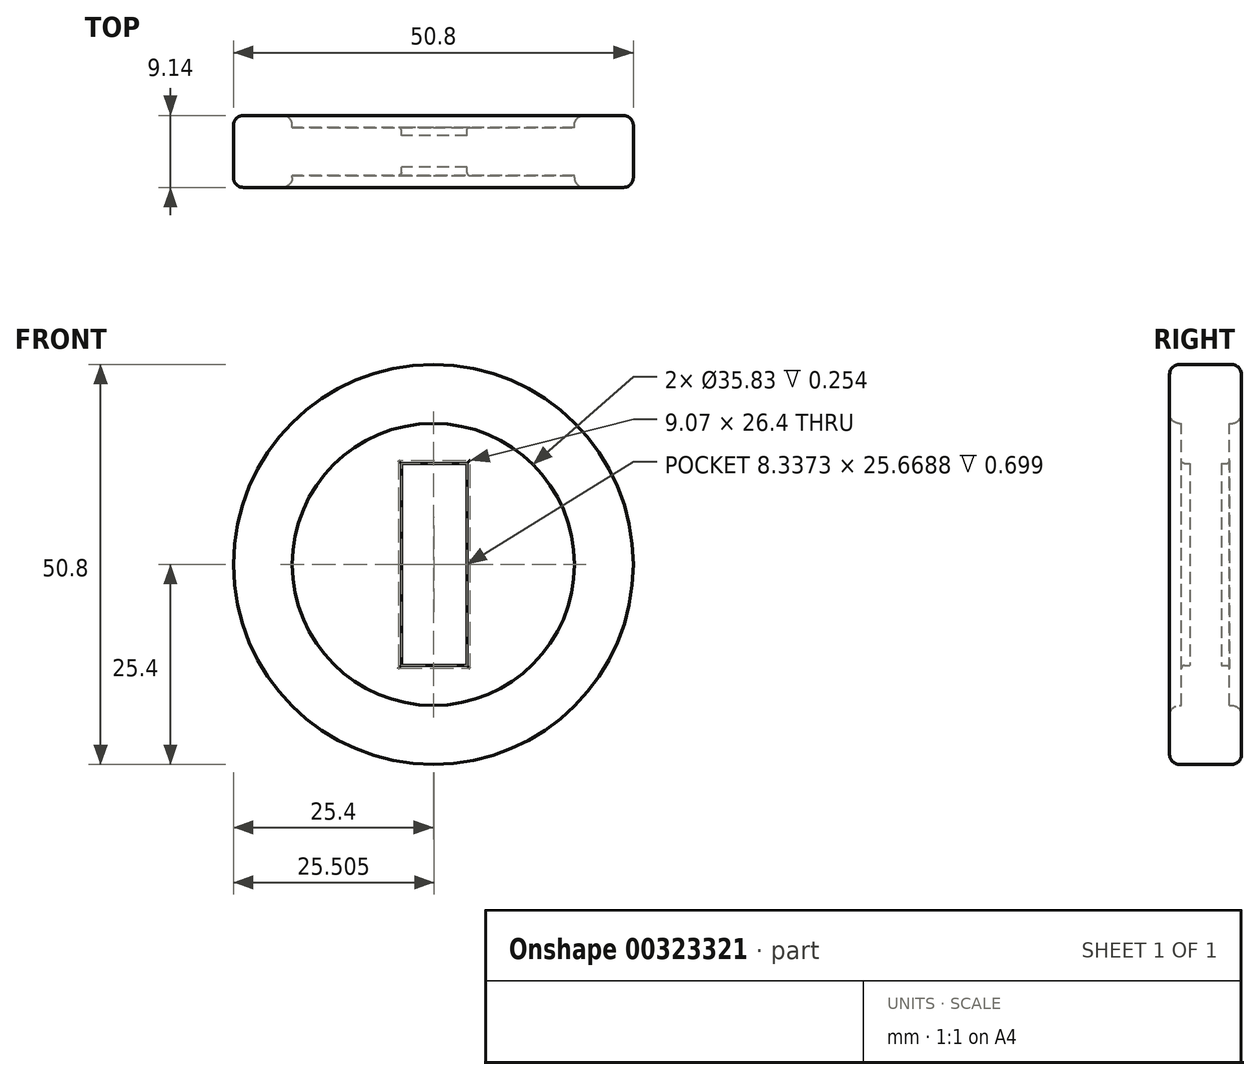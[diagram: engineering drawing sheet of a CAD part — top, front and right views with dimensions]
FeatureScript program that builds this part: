
annotation { "Feature Type Name" : "Feature", "Feature Type Description" : "" }
export const myFeature = defineFeature(function(context is Context, id is Id, definition is map)
    precondition{}
    {
        {
            var Q0;
            Q0=qCreatedBy(makeId("Front.planeOp"),FACE);
            var sketch = newSketch(context, id + "F0", { "sketchPlane" : qUnion([Q0])});
            skCircle(sketch, "E0", {"center": v(0, 0) * mm, "radius": 25.4 * mm});
            skCircle(sketch, "E1", {"center": v(0, 0) * mm, "radius": 17.91 * mm});
            skLineSegment(sketch, "E2", {"start": v(-4.06, 12.83) * mm, "end": v(-4.06, -12.83) * mm});
            skLineSegment(sketch, "E3", {"start": v(-4.06, -12.83) * mm, "end": v(4.27, -12.83) * mm});
            skLineSegment(sketch, "E4", {"start": v(4.27, -12.83) * mm, "end": v(4.27, 12.83) * mm});
            skLineSegment(sketch, "E5", {"start": v(4.27, 12.83) * mm, "end": v(-4.06, 12.83) * mm});
            skSolve(sketch);
        }
        {
            var Q0;
            Q0=makeQuery(id+"F0.imprint","IMPRINT",FACE,{"disambiguationData":[TD([[makeQuery(id+"F0.imprint","IMPRINT",EDGE,{"derivedFrom":sQuery(id+"F0.wireOp",EDGE,"E0")}),1.0]])]});
            extrude(context, id + "F1", {"entities" : qUnion([Q0]), "depth" : 4.57 * mm});
        }
        {
            var Q0;
            Q0=makeQuery(id+"F1.opExtrude","CAP_FACE",FACE,{"disambiguationData":[OSD([sQuery(id+"F0.wireOp",EDGE,"E0"),sQuery(id+"F0.wireOp",EDGE,"E1")])],"isStart":true});
            extrude(context, id + "F2", {"entities" : qUnion([Q0]), "operationType" : NewBodyOperationType.ADD, "depth" : 4.57 * mm});
        }
        {
            var Q0;
            Q0=makeQuery(id+"F0.imprint","IMPRINT",FACE,{"disambiguationData":[TD([[makeQuery(id+"F0.imprint","IMPRINT",EDGE,{"derivedFrom":sQuery(id+"F0.wireOp",EDGE,"E1")}),1.0]])]});
            extrude(context, id + "F3", {"entities" : qUnion([Q0]), "operationType" : NewBodyOperationType.ADD, "depth" : 3.05 * mm});
        }
        {
            var Q0;
            Q0=makeQuery(id+"F0.imprint","IMPRINT",FACE,{"disambiguationData":[TD([[makeQuery(id+"F0.imprint","IMPRINT",EDGE,{"derivedFrom":sQuery(id+"F0.wireOp",EDGE,"E1")}),1.0]])]});
            extrude(context, id + "F4", {"entities" : qUnion([Q0]), "operationType" : NewBodyOperationType.ADD, "oppositeDirection" : true, "depth" : 3.05 * mm});
        }
        {
            var Q0;
            Q0=makeQuery(id+"F0.imprint","IMPRINT",FACE,{"disambiguationData":[TD([[makeQuery(id+"F0.imprint","IMPRINT",EDGE,{"derivedFrom":sQuery(id+"F0.wireOp",EDGE,"E2")}),1.0]])]});
            extrude(context, id + "F5", {"entities" : qUnion([Q0]), "operationType" : NewBodyOperationType.ADD, "depth" : 1.98 * mm});
        }
        {
            var Q0;
            Q0=makeQuery(id+"F0.imprint","IMPRINT",FACE,{"disambiguationData":[TD([[makeQuery(id+"F0.imprint","IMPRINT",EDGE,{"derivedFrom":sQuery(id+"F0.wireOp",EDGE,"E2")}),1.0]])]});
            extrude(context, id + "F6", {"entities" : qUnion([Q0]), "operationType" : NewBodyOperationType.ADD, "oppositeDirection" : true, "depth" : 1.98 * mm});
        }
        {
            var Q0;
            Q0=makeQuery(id+"F2.opExtrude","CAP_EDGE",EDGE,{"disambiguationData":[OSD([sQuery(id+"F0.wireOp",EDGE,"E1")])],"isStart":false});
            var Q1;
            Q1=makeQuery(id+"F2.opExtrude","CAP_EDGE",EDGE,{"disambiguationData":[OSD([sQuery(id+"F0.wireOp",EDGE,"E0")])],"isStart":false});
            var Q2;
            Q2=makeQuery(id+"F1.opExtrude","CAP_EDGE",EDGE,{"disambiguationData":[OSD([sQuery(id+"F0.wireOp",EDGE,"E0")])],"isStart":false});
            var Q3;
            Q3=makeQuery(id+"F1.opExtrude","CAP_EDGE",EDGE,{"disambiguationData":[OSD([sQuery(id+"F0.wireOp",EDGE,"E1")])],"isStart":false});
            fillet(context, id + "F7", {"entities" : qUnion([Q0, Q1, Q2, Q3]), "radius" : 1.27 * mm, "tangentPropagation" : true, "allowEdgeOverflow" : false});
        }
        {
            var Q0;
            Q0=makeQuery(id+"F4.opExtrude","CAP_EDGE",EDGE,{"disambiguationData":[OSD([sQuery(id+"F0.wireOp",EDGE,"E3")])],"isStart":false});
            var Q1;
            Q1=makeQuery(id+"F4.opExtrude","CAP_EDGE",EDGE,{"disambiguationData":[OSD([sQuery(id+"F0.wireOp",EDGE,"E4")])],"isStart":false});
            var Q2;
            Q2=makeQuery(id+"F4.opExtrude","CAP_EDGE",EDGE,{"disambiguationData":[OSD([sQuery(id+"F0.wireOp",EDGE,"E5")])],"isStart":false});
            var Q3;
            Q3=makeQuery(id+"F4.opExtrude","CAP_EDGE",EDGE,{"disambiguationData":[OSD([sQuery(id+"F0.wireOp",EDGE,"E2")])],"isStart":false});
            var Q4;
            Q4=makeQuery(id+"F3.opExtrude","CAP_EDGE",EDGE,{"disambiguationData":[OSD([sQuery(id+"F0.wireOp",EDGE,"E2")])],"isStart":false});
            var Q5;
            Q5=makeQuery(id+"F3.opExtrude","CAP_EDGE",EDGE,{"disambiguationData":[OSD([sQuery(id+"F0.wireOp",EDGE,"E5")])],"isStart":false});
            var Q6;
            Q6=makeQuery(id+"F3.opExtrude","CAP_EDGE",EDGE,{"disambiguationData":[OSD([sQuery(id+"F0.wireOp",EDGE,"E4")])],"isStart":false});
            var Q7;
            Q7=makeQuery(id+"F3.opExtrude","CAP_EDGE",EDGE,{"disambiguationData":[OSD([sQuery(id+"F0.wireOp",EDGE,"E3")])],"isStart":false});
            fillet(context, id + "F8", {"entities" : qUnion([Q0, Q1, Q2, Q3, Q4, Q5, Q6, Q7]), "radius" : 0.37 * mm, "tangentPropagation" : true, "allowEdgeOverflow" : false});
        }
    });
